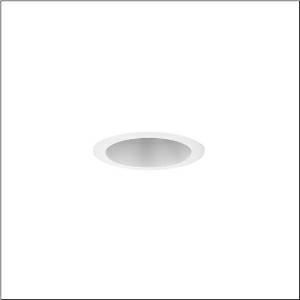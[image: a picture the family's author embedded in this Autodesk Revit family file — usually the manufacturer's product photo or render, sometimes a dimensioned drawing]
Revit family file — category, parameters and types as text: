
# Revit family: lunis_31-l_51dn16me41b
name_source: partatom
category: Lighting Fixtures
units: mm (PartAtom-declared; Revit-internal decimal feet)

## family parameters
Cut with Voids When Loaded = No
Host = Face
Light Source = No
Part Type = Normal
Room Calculation Point = No
Round Connector Dimension = Use Diameter
Shared = No

## types (1)
- --- (1 x LED, 1650 lm, 11.5 W, 4000K)
    Apparent Load = 12 VA
    CIE Flux Codes = 76 93 99 100 100
    Color Rendering = 80
    Color Temperature = 4000K
    Default Elevation = 1800 mm
    Description = Lunis 31, -L, downlight, light control with reflector, light emission: direct distribution, LED rated luminous flux: 1.650lm, light colour: 840, mains connection: 220..240V, AC, 50/60Hz, housing, of aluminium, white, protection rating (complete): IP20, protection rating (on room side): IP54, insulation class (complete): insulation class II (safety insulation), certification: CE, packaging unit: 1 piece
    Height = 0 mm  [stored 0 ft]
    Lamp = 1 x LED
    Lamp Light Flux = 1650 lm
    Lamp Power = 11.5 W
    Lamp count = 1
    Length = 188 mm  [stored 0.616798 ft]
    Luminous efficacy = 143 lm/W
    Manufacturer = Siteco
    ModVariant = No
    Model = 51DN16ME41B
    Mounting Place = Ceiling
    Mounting Type = Recessed
    Number of Poles = 1
    OnlyDefault = Yes
    Power Factor = 1
    Product Name = Lunis 31-L
    Product group = downlight
    ProductGroupID = 400
    Protection Class = Protection class II
    Protection Degree = IP 20
    RLX_Detail_Level = 1
    RLX_Emergency_Light_Flux = 0 lm
    RLX_Emergency_Type = 0
    RLX_Emergency_Type_DB = No
    RlxData = <blob elided: 22557 chars, md5=5282ebd2>
    Socket = socket
    Standby Power = 0 W
    System Light Flux = 1650 lm
    System Power = 12 W
    Type Comments = individual setting: luminous flux: 100 % | (OFF | ON) | 300 mA
    Type Image = l_1345911.jpg
    URL = http://relux.com
    VarID = @adj_010167
    Voltage = 0 V
    Weight = 0.00 kg
    Width = 0 mm  [stored 0 ft]

note: [stored X ft] marks values corroborated as IEEE doubles in the binary element streams (Revit-internal decimal feet)

## geometry (parser evidence)
native form markers: Blend x4, Sweep x12
no freeform markers — native parametric forms only
